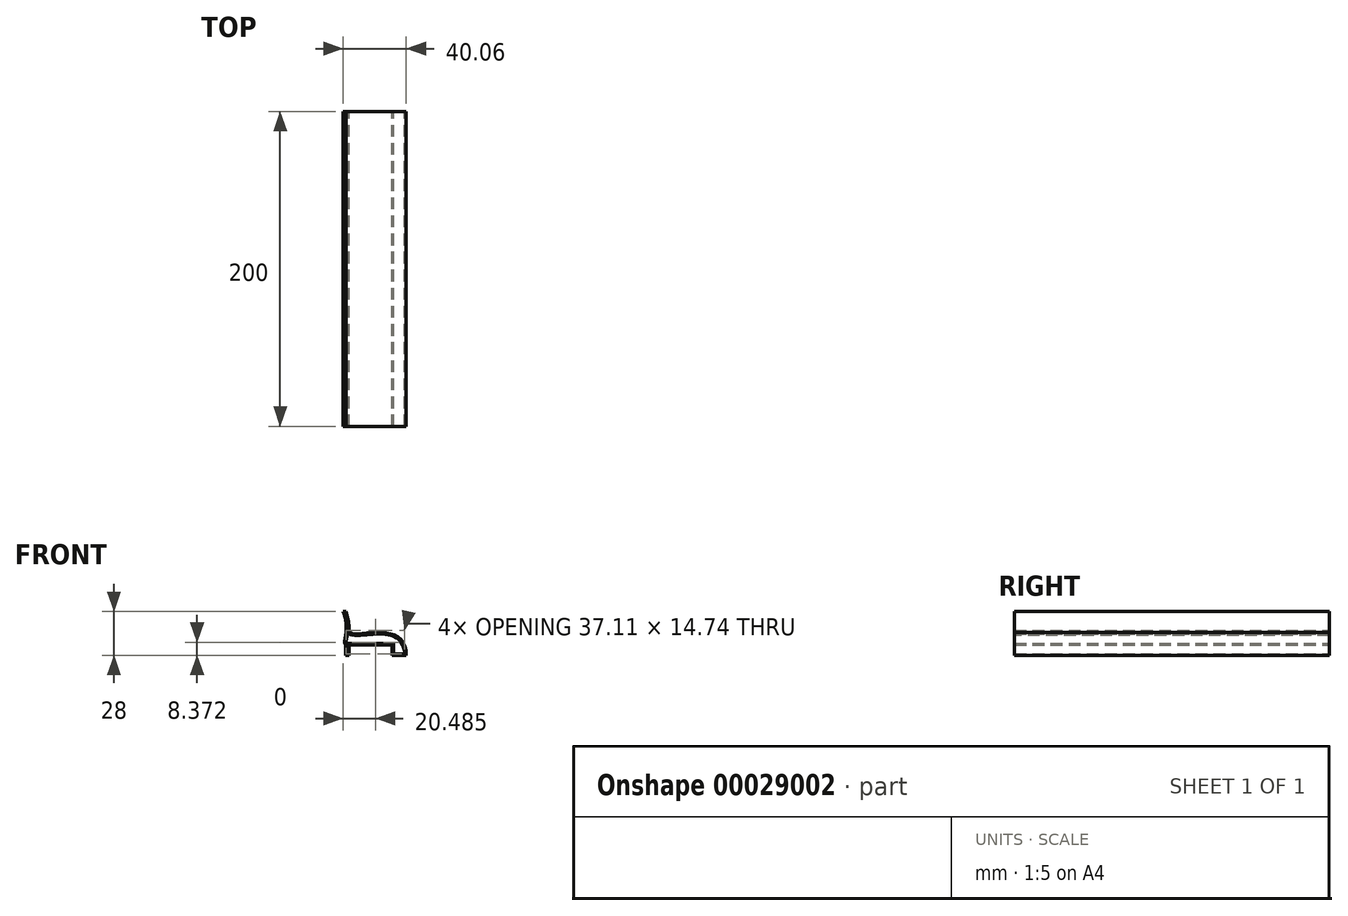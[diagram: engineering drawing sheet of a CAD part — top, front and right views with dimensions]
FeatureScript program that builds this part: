
annotation { "Feature Type Name" : "Feature", "Feature Type Description" : "" }
export const myFeature = defineFeature(function(context is Context, id is Id, definition is map)
    precondition{}
    {
        {
            var Q0;
            Q0=qCreatedBy(makeId("Front.planeOp"),FACE);
            var sketch = newSketch(context, id + "F0", { "sketchPlane" : qUnion([Q0])});
            skFitSpline(sketch, "E0", {"points": [v(0, 0) * mm, v(-11.76, 14.22) * mm, v(-34.82, 14.09) * mm, v(-38.34, 28) * mm], "startDerivative": vector(0, 76.5) * mm, "endDerivative": vector(-34.58, 94.97) * mm});
            skLineSegment(sketch, "E1", {"start": v(-38.34, 28) * mm, "end": v(-40.06, 28) * mm});
            skLineSegment(sketch, "E2", {"start": v(-38.5, 0) * mm, "end": v(-36.48, 0) * mm});
            skLineSegment(sketch, "E3", {"start": v(-36.48, 0) * mm, "end": v(-36.48, 6.72) * mm});
            skLineSegment(sketch, "E4", {"start": v(-36.48, 6.72) * mm, "end": v(-9.16, 6.72) * mm});
            skLineSegment(sketch, "E5", {"start": v(-9.16, 6.72) * mm, "end": v(-9.16, 0) * mm});
            skLineSegment(sketch, "E6", {"start": v(-9.16, 0) * mm, "end": v(0, 0) * mm});
            skFitSpline(sketch, "E7", {"points": [v(-40.06, 28) * mm, v(-38.27, 20.74) * mm, v(-38.34, 13.64) * mm, v(-38.5, 6.73) * mm], "startDerivative": vector(12.32, -41.35) * mm, "endDerivative": vector(11.74, -16.22) * mm});
            skLineSegment(sketch, "E8", {"start": v(-38.5, 6.73) * mm, "end": v(-38.5, 0) * mm});
            skSolve(sketch);
        }
        {
            var Q0;
            Q0 = qSketchRegion(id + "F0", true);
            extrude(context, id + "F1", {"entities" : qUnion([Q0]), "depth" : 200 * mm});
        }
        {
            var Q0;
            Q0=makeQuery(id+"F1.opExtrude","CAP_FACE",FACE,{"disambiguationData":[OSD([sQuery(id+"F0.wireOp",EDGE,"E0"),sQuery(id+"F0.wireOp",EDGE,"E1"),sQuery(id+"F0.wireOp",EDGE,"dd3ac620-297f-45c8-a4bd-335832dadb35"),sQuery(id+"F0.wireOp",EDGE,"E2"),sQuery(id+"F0.wireOp",EDGE,"E3"),sQuery(id+"F0.wireOp",EDGE,"E4"),sQuery(id+"F0.wireOp",EDGE,"E5"),sQuery(id+"F0.wireOp",EDGE,"E6")])],"isStart":false});
            var Q1;
            Q1=makeQuery(id+"F1.opExtrude","CAP_FACE",FACE,{"disambiguationData":[OSD([sQuery(id+"F0.wireOp",EDGE,"E0"),sQuery(id+"F0.wireOp",EDGE,"E1"),sQuery(id+"F0.wireOp",EDGE,"dd3ac620-297f-45c8-a4bd-335832dadb35"),sQuery(id+"F0.wireOp",EDGE,"E2"),sQuery(id+"F0.wireOp",EDGE,"E3"),sQuery(id+"F0.wireOp",EDGE,"E4"),sQuery(id+"F0.wireOp",EDGE,"E5"),sQuery(id+"F0.wireOp",EDGE,"E6")])],"isStart":true});
            shell(context, id + "F2", {"entities" : qUnion([Q0, Q1]), "thickness" : 1 * mm});
        }
    });
